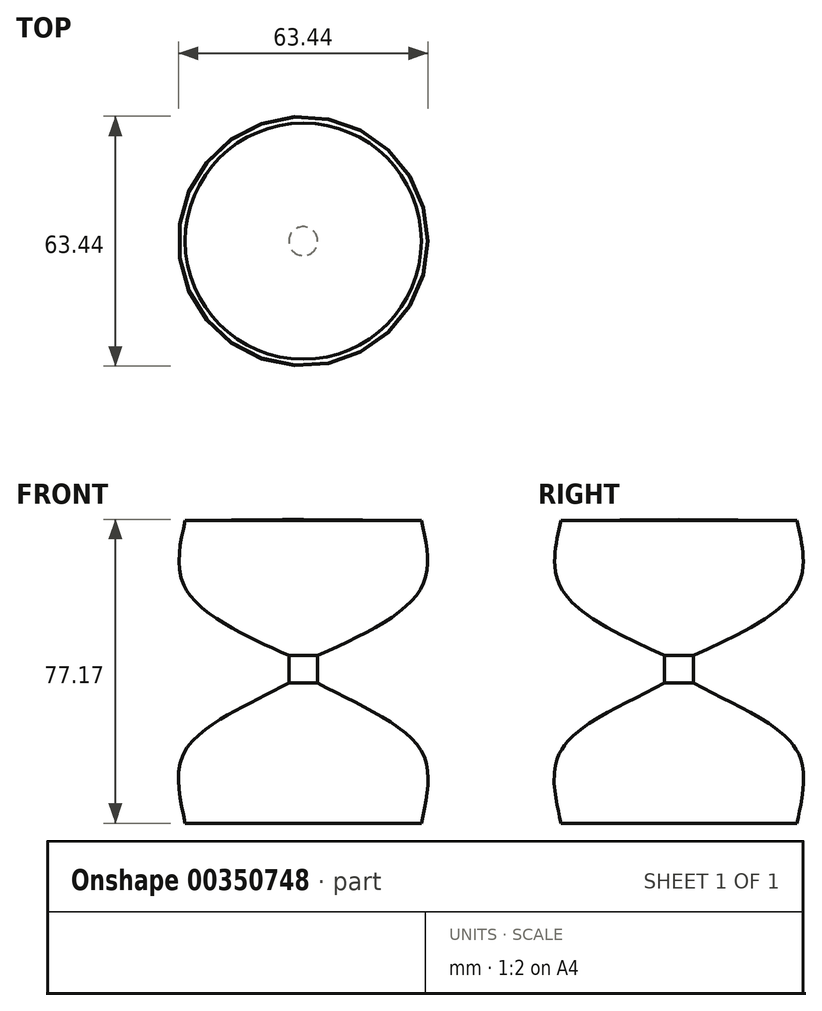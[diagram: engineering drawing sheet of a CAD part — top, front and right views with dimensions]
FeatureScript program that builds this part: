
annotation { "Feature Type Name" : "Feature", "Feature Type Description" : "" }
export const myFeature = defineFeature(function(context is Context, id is Id, definition is map)
    precondition{}
    {
        {
            var Q0;
            Q0=qCreatedBy(makeId("Front.planeOp"),FACE);
            var sketch = newSketch(context, id + "F0", { "sketchPlane" : qUnion([Q0])});
            skLineSegment(sketch, "E0", {"start": v(0, 38.66) * mm, "end": v(0, -38.5) * mm});
            skLineSegment(sketch, "E1", {"start": v(0, -38.5) * mm, "end": v(30, -38.5) * mm});
            skLineSegment(sketch, "E2", {"start": v(3.67, -2.86) * mm, "end": v(3.67, 4.06) * mm});
            skLineSegment(sketch, "E3", {"start": v(30, 38.36) * mm, "end": v(0, 38.66) * mm});
            skFitSpline(sketch, "E4", {"points": [v(30, -38.5) * mm, v(30, -20.11) * mm, v(3.67, -2.86) * mm], "startDerivative": vector(9, 43.4) * mm, "endDerivative": vector(-51.39, 28.44) * mm});
            skFitSpline(sketch, "E5", {"points": [v(30, 38.36) * mm, v(30, 21.3) * mm, v(3.67, 4.06) * mm], "startDerivative": vector(9.7, -42.41) * mm, "endDerivative": vector(-58.87, -26.97) * mm});
            skSolve(sketch);
        }
        {
            var Q0;
            Q0=makeQuery(id+"F0.imprint","IMPRINT",FACE,{"disambiguationData":[TD([[makeQuery(id+"F0.imprint","IMPRINT",EDGE,{"derivedFrom":sQuery(id+"F0.wireOp",EDGE,"E0")}),1.0]])]});
            var Q1;
            Q1=sQuery(id+"F0.wireOp",EDGE,"E0");
            revolve(context, id + "F1", {"entities" : qUnion([Q0]), "axis" : qUnion([Q1]), "revolveType" : RevolveType.FULL});
        }
    });
